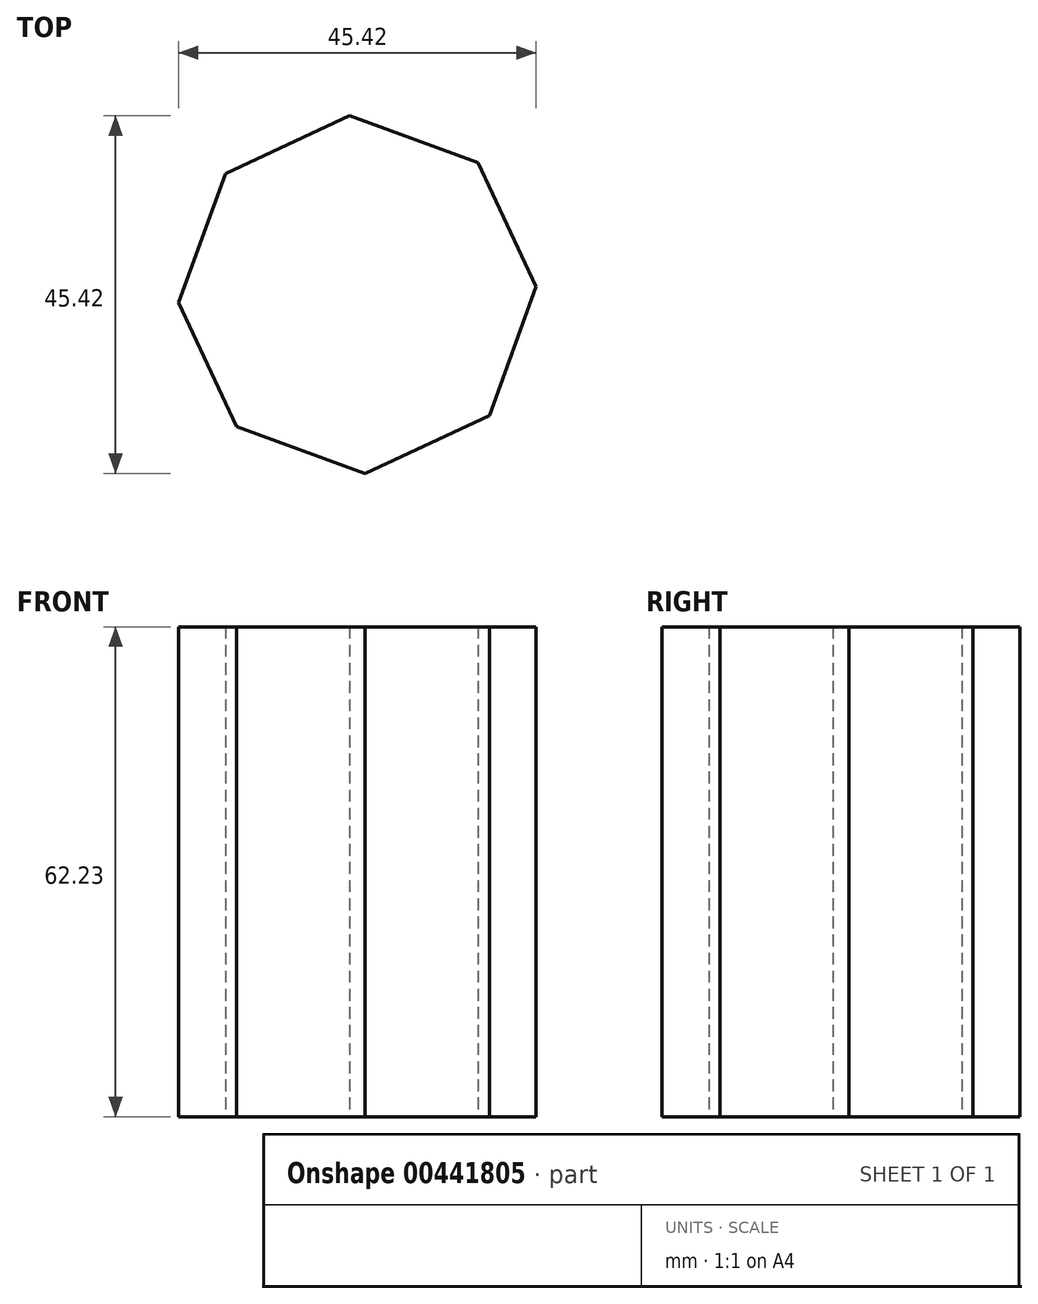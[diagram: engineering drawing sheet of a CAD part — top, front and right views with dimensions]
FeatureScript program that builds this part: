
annotation { "Feature Type Name" : "Feature", "Feature Type Description" : "" }
export const myFeature = defineFeature(function(context is Context, id is Id, definition is map)
    precondition{}
    {
        {
            var Q0;
            Q0=qCreatedBy(makeId("Top.planeOp"),FACE);
            var sketch = newSketch(context, id + "F0", { "sketchPlane" : qUnion([Q0])});
            skCircle(sketch, "E0.cCircle", {"center": v(-48.83, 46.01) * mm, "radius": 21 * mm, "construction": true});
            skLineSegment(sketch, "E0.0", {"start": v(-26.12, 47.01) * mm, "end": v(-32.07, 30.66) * mm});
            skLineSegment(sketch, "E0.1", {"start": v(-32.07, 30.66) * mm, "end": v(-47.83, 23.3) * mm});
            skLineSegment(sketch, "E0.2", {"start": v(-47.83, 23.3) * mm, "end": v(-64.19, 29.25) * mm});
            skLineSegment(sketch, "E0.3", {"start": v(-64.19, 29.25) * mm, "end": v(-71.54, 45.01) * mm});
            skLineSegment(sketch, "E0.4", {"start": v(-71.54, 45.01) * mm, "end": v(-65.6, 61.37) * mm});
            skLineSegment(sketch, "E0.5", {"start": v(-65.6, 61.37) * mm, "end": v(-49.83, 68.72) * mm});
            skLineSegment(sketch, "E0.6", {"start": v(-49.83, 68.72) * mm, "end": v(-33.48, 62.78) * mm});
            skLineSegment(sketch, "E0.7", {"start": v(-33.48, 62.78) * mm, "end": v(-26.12, 47.01) * mm});
            skPoint(sketch, "E0.0.midPoint", {"position": v(-29.1, 38.83) * mm});
            skSolve(sketch);
        }
        {
            var Q0;
            Q0=makeQuery(id+"F0.imprint","IMPRINT",FACE,{"disambiguationData":[TD([[makeQuery(id+"F0.imprint","IMPRINT",EDGE,{"derivedFrom":sQuery(id+"F0.wireOp",EDGE,"E0.0")}),-1.0]])]});
            extrude(context, id + "F1", {"entities" : qUnion([Q0]), "depth" : 62.23 * mm});
        }
    });
